# Revit family: Domotics-DomesticRanges-GEWISS-SYSTEM_SIGNALLING-LAMP_1M
name_source: partatom
category: Apparecchi elettrici
revit_build: Autodesk Revit 2016 (Build: 20161004_0715(x64)
units: mm (PartAtom-declared; Revit-internal decimal feet)

## family parameters
Condiviso = Sì
Host = Superficie
Mantenere orientamento annotazione = Sì
Punto di calcolo locali = Sì
Quota connettore circolare = Usa diametro
Taglio con vuoti quando caricato = Sì
Tipo di parte = Normale

## types (10) — shared parameters
Carico apparente = 0 VA
Catalogue = DOMOTICS
Catalogue Range = SYSTEM - DOMESTIC RANGE
Description. = Flat indicator lamp
Diffusor type = Flat
Electrocod = 0132
Fixing for lamp = Cartridge
IDF = fa61e156-ee9e-44cf-9531-f9ff91addf2c
IDT = e934abc8-67f1-4d65-9d07-b179970d7e55
Immagine tipo = GW21631.jpg
Lamp holder = Cartridge
N. poli = 1
No. SYSTEM modules = 1
Produttore = GEWISS S.p.A.
Prospetto di default = 1219 mm
SEO = Indicator
TIPO_ = System Spie 1M_GENERICO : GW21631 Spia piana diffusore azzurro nero
Technical sheet = https://www.gewiss.com
Type = Single
Type: = Single
URL = https://www.gewiss.com
Version file RFA = 19.4
Volt = 230 V
Voltage = 12/24/250V AC
Voltage: = 12/24/250V AC

## per-type parameters (varying)
| type | Colour | Descrizione | Diffuser colour | Diffuser colour: | Diffuser meaning | EAN code | Modello |
| GW21603 - Ind.light-red flat diff. black | Black | IND.LIGHT-RED FLAT DIFF.SY/BK | Red | Red | Danger | 8011564129696 | GW21603 |
| GW20604 - Ind.light-green flat diff. white | White | IND.LIGHT-GREEN FLAT DIFF.SY/WT | Green | Green | Safety | 8011564000933 | GW20604 |
| GW20605 - Ind.light-yellow flat diff. white | White | IND.LIGHT-YELLOW FLAT DIFF.SY/WT | Yellow | Yellow | Attention | 8011564000940 | GW20605 |
| GW20606 - Ind.light-transp.flat diff. white | White | IND.LIGHT-TRANSP.FLAT DIFF.SY/WT | Transparent | Transparent | Neutral | 8011564000957 | GW20606 |
| GW21606 - Ind.light-transp.flat diff. black | Black | IND.LIGHT-TRANSP.FLAT DIFF.SY/BK | Transparent | Transparent | Neutral | 8011564129726 | GW21606 |
| GW20631 - Ind.light-blue flat diff. white | White | IND.LIGHT-BLUE FLAT DIFF.SY/WT | Light blue | Light blue | Specific | 8011564024830 | GW20631 |
| GW20603 - Ind.light-red flat diff. white | White | IND.LIGHT-RED FLAT DIFF.SY/WT | Red | Red | Danger | 8011564000926 | GW20603 |
| GW21631 - Ind.light-blue flat diff. black | Black | IND.LIGHT-BLUE FLAT DIFF.SY/BK | Light blue | Light blue | Specific | 8011564129733 | GW21631 |
| GW21605 - Ind.light-yellow flat diff. black | Black | IND.LIGHT-YELLOW FLAT DIFF.SY/BK | Yellow | Yellow | Attention | 8011564129719 | GW21605 |
| GW21604 - Ind.light-green flat diff. black | Black | IND.LIGHT-GREEN FLAT DIFF.SY/BK | Green | Green | Safety | 8011564129702 | GW21604 |

## geometry (parser evidence)
native form markers: Sweep x2
no freeform markers — native parametric forms only
